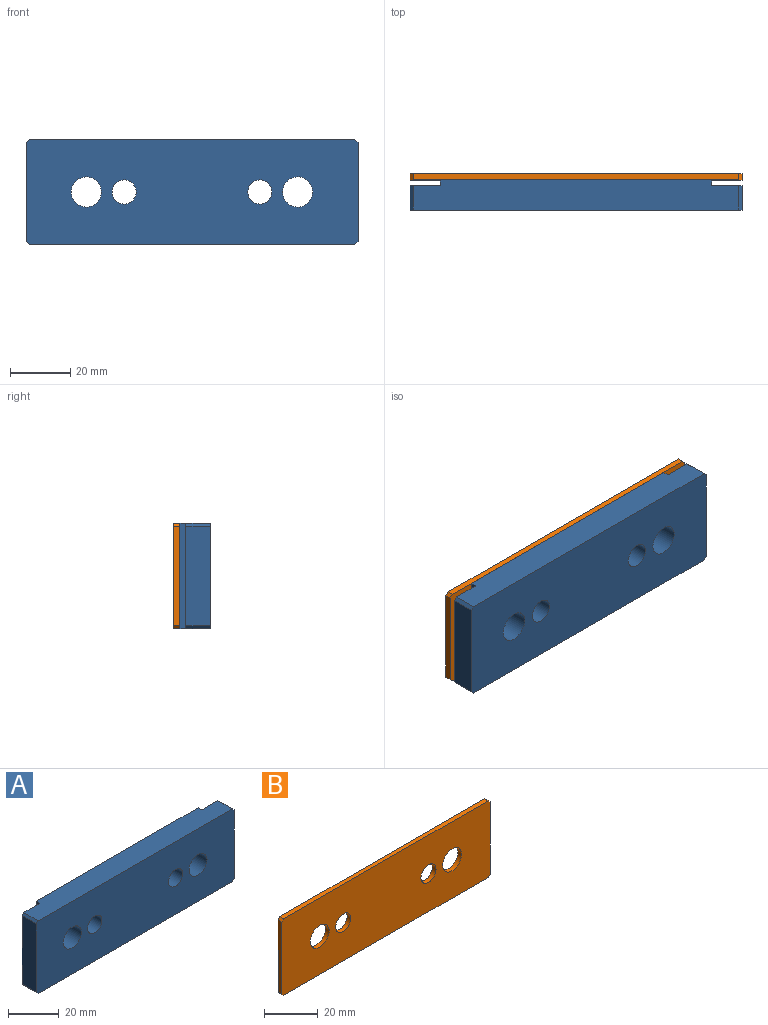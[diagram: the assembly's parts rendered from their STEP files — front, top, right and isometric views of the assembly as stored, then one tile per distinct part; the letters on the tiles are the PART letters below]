
ASSEMBLY  parts=2 mates=1
PART A: 20 faces, bbox 110x10x35 mm
  f0: plane 35.01x9.8mm, normal (0,1,0), area 342.1mm2, adj f1,f2,f7,f14,f15,f19
  f1: plane 33.01x8mm, normal (-1,0,0), area 264.1mm2, adj f0,f10,f14,f15
  f2: plane 108x10mm, normal (0,0,-1), area 1044mm2, adj f0,f9,f10,f11,f12,f13,f15,f17
  f3: plane 33.01x8mm, normal (1,0,0), area 264.1mm2, adj f9,f10,f16,f17
  f4: cylinder r=4mm len=10mm, axis (0,-1,0), area 251.3mm2, adj f10,f13
  f5: cylinder r=5mm len=10mm, axis (0,-1,0), area 314.2mm2, adj f10,f13
  f6: cylinder r=4mm len=10mm, axis (0,-1,0), area 251.3mm2, adj f10,f13
  f7: plane 108x10mm, normal (0,0,1), area 1044mm2, adj f0,f9,f10,f11,f12,f13,f14,f16
  f8: cylinder r=5mm len=10mm, axis (0,-1,0), area 314.2mm2, adj f10,f13
  f9: plane 35.01x9.8mm, normal (0,1,0), area 342.1mm2, adj f2,f3,f7,f16,f17,f18
  f10: plane 110x35.01mm, normal (0,-1,0), area 3591.6mm2, adj f1,f2,f3,f4,f5,f6,f7,f8
  f11: plane 35.01x1.8mm, normal (1,0,0), area 63mm2, adj f2,f7,f13,f18
  f12: plane 35.01x1.8mm, normal (-1,0,0), area 63mm2, adj f2,f7,f13,f19
  f13: plane 90x35.01mm, normal (0,1,0), area 2893.4mm2, adj f2,f4,f5,f6,f7,f8,f11,f12
  f14: plane 8x1mm, normal (-0.71,0,0.71), area 11.3mm2, adj f0,f1,f7,f10
  f15: plane 8x1mm, normal (-0.71,0,-0.71), area 11.3mm2, adj f0,f1,f2,f10
  f16: plane 8x1mm, normal (0.71,0,0.71), area 11.3mm2, adj f3,f7,f9,f10
  f17: plane 8x1mm, normal (0.71,0,-0.71), area 11.3mm2, adj f2,f3,f9,f10
  f18: cylinder r=0.2mm len=35.01mm, axis (0,0,1), area 11mm2, adj f2,f7,f9,f11
  f19: cylinder r=0.2mm len=35.01mm, axis (0,0,-1), area 11mm2, adj f0,f2,f7,f12
PART B: 14 faces, bbox 110x2x35 mm
  f0: plane 33.01x2mm, normal (-1,0,0), area 66mm2, adj f8,f9,f10,f11
  f1: plane 108x2mm, normal (0,0,-1), area 216mm2, adj f8,f9,f11,f12
  f2: plane 33.01x2mm, normal (1,0,0), area 66mm2, adj f8,f9,f12,f13
  f3: cylinder r=4mm len=8mm, axis (0,-1,0), area 50.3mm2, adj f8,f9
  f4: cylinder r=5mm len=10mm, axis (0,-1,0), area 62.8mm2, adj f8,f9
  f5: cylinder r=4mm len=8mm, axis (0,-1,0), area 50.3mm2, adj f8,f9
  f6: plane 108x2mm, normal (0,0,1), area 216mm2, adj f8,f9,f10,f13
  f7: cylinder r=5mm len=10mm, axis (0,-1,0), area 62.8mm2, adj f8,f9
  f8: plane 110x35.01mm, normal (0,1,0), area 3591.6mm2, adj f0,f1,f2,f3,f4,f5,f6,f7
  f9: plane 110x35.01mm, normal (0,-1,0), area 3591.6mm2, adj f0,f1,f2,f3,f4,f5,f6,f7
  f10: plane 2x1mm, normal (-0.71,0,0.71), area 2.8mm2, adj f0,f6,f8,f9
  f11: plane 2x1mm, normal (-0.71,0,-0.71), area 2.8mm2, adj f0,f1,f8,f9
  f12: plane 2x1mm, normal (0.71,0,-0.71), area 2.8mm2, adj f1,f2,f8,f9
  f13: plane 2x1mm, normal (0.71,0,0.71), area 2.8mm2, adj f2,f6,f8,f9
PLACE A at identity
PLACE B t=(0,10,0)mm
MATE fastened B.f4 <-> A.f5  axis (0,-1,0) through (-35,10,0)mm
